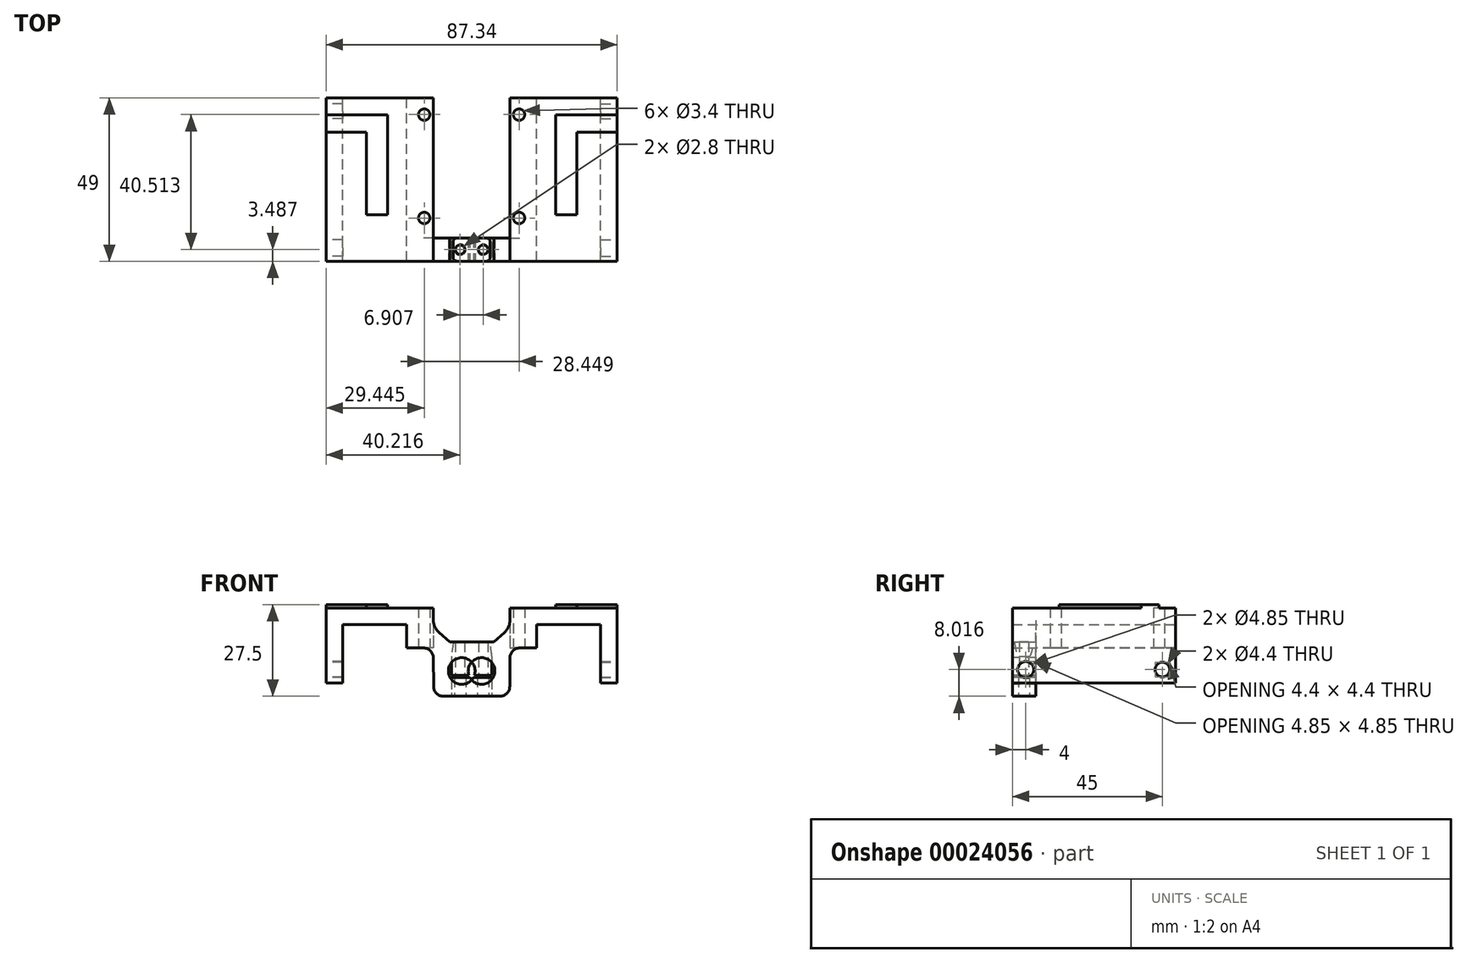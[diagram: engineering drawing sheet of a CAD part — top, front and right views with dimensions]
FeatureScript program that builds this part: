
annotation { "Feature Type Name" : "Feature", "Feature Type Description" : "" }
export const myFeature = defineFeature(function(context is Context, id is Id, definition is map)
    precondition{}
    {
        {
            var Q0;
            Q0=qCreatedBy(makeId("Front.planeOp"),FACE);
            var sketch = newSketch(context, id + "F0", { "sketchPlane" : qUnion([Q0])});
            skLineSegment(sketch, "E0", {"start": v(-18.67, 7.33) * mm, "end": v(-18.67, 29.8) * mm});
            skLineSegment(sketch, "E1", {"start": v(-18.67, 29.8) * mm, "end": v(13.53, 29.8) * mm});
            skLineSegment(sketch, "E2", {"start": v(13.53, 29.8) * mm, "end": v(13.53, 23.9) * mm});
            skLineSegment(sketch, "E3", {"start": v(5.53, 17.8) * mm, "end": v(5.53, 24.8) * mm});
            skLineSegment(sketch, "E4", {"start": v(5.53, 24.8) * mm, "end": v(-13.67, 24.8) * mm});
            skLineSegment(sketch, "E5", {"start": v(-13.67, 24.8) * mm, "end": v(-13.67, 7.33) * mm});
            skLineSegment(sketch, "E6", {"start": v(-13.67, 7.33) * mm, "end": v(-18.67, 7.33) * mm});
            skLineSegment(sketch, "E7", {"start": v(13.53, 23.9) * mm, "end": v(13.53, 17.8) * mm});
            skLineSegment(sketch, "E8", {"start": v(13.53, 17.8) * mm, "end": v(5.53, 17.8) * mm});
            skLineSegment(sketch, "E9", {"start": v(13.53, 23.9) * mm, "end": v(13.53, 23.9) * mm});
            skLineSegment(sketch, "E10", {"start": v(31.08, 15.31) * mm, "end": v(31.08, 9.01) * mm});
            skLineSegment(sketch, "E11", {"start": v(31.08, 9.01) * mm, "end": v(23.88, 9.01) * mm});
            skLineSegment(sketch, "E12", {"start": v(23.88, 9.61) * mm, "end": v(23.88, 9.01) * mm});
            skLineSegment(sketch, "E13", {"start": v(23.88, 9.61) * mm, "end": v(31.08, 9.61) * mm});
            skLineSegment(sketch, "E14", {"start": v(31.08, 9.61) * mm, "end": v(31.08, 3.31) * mm});
            skLineSegment(sketch, "E15", {"start": v(31.08, 3.31) * mm, "end": v(13.58, 3.31) * mm});
            skLineSegment(sketch, "E16", {"start": v(13.58, 3.31) * mm, "end": v(13.53, 17.8) * mm});
            skLineSegment(sketch, "E17", {"start": v(31.08, 15.31) * mm, "end": v(23.28, 15.31) * mm});
            skLineSegment(sketch, "E18", {"start": v(23.28, 15.31) * mm, "end": v(13.53, 23.9) * mm});
            skLineSegment(sketch, "E19", {"start": v(18.4, 19.61) * mm, "end": v(30.5, 19.61) * mm});
            skPoint(sketch, "E19.endSnap0", {"position": v(18.4, 19.61) * mm});
            skLineSegment(sketch, "E20", {"start": v(30.5, 19.61) * mm, "end": v(31.08, 15.31) * mm});
            skSolve(sketch);
        }
        {
            var Q0;
            Q0=makeQuery(id+"F0.imprint","IMPRINT",FACE,{"disambiguationData":[TD([[makeQuery(id+"F0.imprint","IMPRINT",EDGE,{"derivedFrom":sQuery(id+"F0.wireOp",EDGE,"E0")}),-1.0]])]});
            var Q1;
            {var subQ2=sQuery(id+"F0.wireOp",EDGE,"69cbcc5d-e0c3-48db-8baf-3487a8abab7d");Q1=makeQuery(id+"F0.imprint","IMPRINT",FACE,{"disambiguationData":[TD([[makeQuery(id+"F0.imprint","IMPRINT",EDGE,{"derivedFrom":subQ2}),-1.0]])]});}
            var Q2;
            Q2=makeQuery(id+"F0.imprint","IMPRINT",FACE,{"disambiguationData":[TD([[makeQuery(id+"F0.imprint","IMPRINT",EDGE,{"derivedFrom":sQuery(id+"F0.wireOp",EDGE,"E7")}),1.0]])]});
            var Q3;
            {var subQ2=sQuery(id+"F0.wireOp",EDGE,"E17");Q3=makeQuery(id+"F0.imprint","IMPRINT",FACE,{"disambiguationData":[TD([[makeQuery(id+"F0.imprint","IMPRINT",EDGE,{"derivedFrom":subQ2}),-1.0]])]});}
            extrude(context, id + "F1", {"entities" : qUnion([Q0, Q1, Q2, Q3]), "depth" : 7 * mm});
        }
        {
            var Q0;
            Q0=makeQuery(id+"F0.imprint","IMPRINT",FACE,{"disambiguationData":[TD([[makeQuery(id+"F0.imprint","IMPRINT",EDGE,{"derivedFrom":sQuery(id+"F0.wireOp",EDGE,"E0")}),-1.0]])]});
            extrude(context, id + "F2", {"entities" : qUnion([Q0]), "operationType" : NewBodyOperationType.ADD, "oppositeDirection" : true, "depth" : 42 * mm});
        }
        {
            var Q0;
            {var subQ0=sQuery(id+"F0.wireOp",EDGE,"E8");Q0=makeQuery(id+"F2.boolean.opBoolean","MERGE",FACE,{"derivedFrom":[makeQuery(id+"F1.opExtrude","SWEPT_FACE",FACE,{"disambiguationData":[OSD([subQ0])]}),makeQuery(id+"F2.opExtrude","SWEPT_FACE",FACE,{"disambiguationData":[OSD([subQ0])]})]});}
            var sketch = newSketch(context, id + "F3", { "sketchPlane" : qUnion([Q0])});
            skCircle(sketch, "E21", {"center": v(10.78, -6) * mm, "radius": 1.7 * mm});
            skCircle(sketch, "E22", {"center": v(10.78, -37) * mm, "radius": 1.7 * mm});
            skCircle(sketch, "E23", {"center": v(26.28, -21.5) * mm, "radius": 11 * mm});
            skSolve(sketch);
        }
        {
            var Q0;
            Q0=qSketchRegion(id+"F3",true);
            extrude(context, id + "F4", {"entities" : qUnion([Q0]), "operationType" : NewBodyOperationType.REMOVE, "endBound" : BoundingType.THROUGH_ALL, "oppositeDirection" : true, "depth" : 25 * mm});
        }
        {
            var Q0;
            Q0=makeQuery(id+"F1.opExtrude","CAP_FACE",FACE,{"disambiguationData":[OSD([sQuery(id+"F0.wireOp",EDGE,"E0"),sQuery(id+"F0.wireOp",EDGE,"E1"),sQuery(id+"F0.wireOp",EDGE,"E2"),sQuery(id+"F0.wireOp",EDGE,"E3"),sQuery(id+"F0.wireOp",EDGE,"E4"),sQuery(id+"F0.wireOp",EDGE,"E5"),sQuery(id+"F0.wireOp",EDGE,"E6"),sQuery(id+"F0.wireOp",EDGE,"E8"),sQuery(id+"F0.wireOp",EDGE,"E9"),sQuery(id+"F0.wireOp",EDGE,"58f11638-63e7-4b32-8aff-a1ba3c53649b"),sQuery(id+"F0.wireOp",EDGE,"E10"),sQuery(id+"F0.wireOp",EDGE,"E11"),sQuery(id+"F0.wireOp",EDGE,"E12"),sQuery(id+"F0.wireOp",EDGE,"E13"),sQuery(id+"F0.wireOp",EDGE,"E14"),sQuery(id+"F0.wireOp",EDGE,"E15"),sQuery(id+"F0.wireOp",EDGE,"E16")])],"isStart":false});
            var sketch = newSketch(context, id + "F5", { "sketchPlane" : qUnion([Q0])});
            skCircle(sketch, "E24", {"center": v(22.03, 10.9) * mm, "radius": 4 * mm});
            skSolve(sketch);
        }
        {
            var Q0;
            Q0=qSketchRegion(id+"F5",true);
            extrude(context, id + "F6", {"entities" : qUnion([Q0]), "operationType" : NewBodyOperationType.REMOVE, "oppositeDirection" : true, "depth" : 10 * mm});
        }
        {
            var Q0;
            Q0=qSketchRegion(id+"F3",true);
            extrude(context, id + "F7", {"entities" : qUnion([Q0]), "operationType" : NewBodyOperationType.REMOVE, "endBound" : BoundingType.THROUGH_ALL, "oppositeDirection" : true, "depth" : 25 * mm});
        }
        {
            var Q0;
            Q0=makeQuery(id+"F1.opExtrude","SWEPT_FACE",FACE,{"disambiguationData":[OSD([sQuery(id+"F0.wireOp",EDGE,"E15")])]});
            var sketch = newSketch(context, id + "F8", { "sketchPlane" : qUnion([Q0])});
            skCircle(sketch, "E25", {"center": v(28.45, 3.51) * mm, "radius": 1.7 * mm});
            skCircle(sketch, "E26", {"center": v(28.45, 3.51) * mm, "radius": 1.4 * mm});
            skSolve(sketch);
        }
        {
            var Q0;
            Q0=makeQuery(id+"F8.imprint","IMPRINT",FACE,{"disambiguationData":[TD([[makeQuery(id+"F8.imprint","IMPRINT",EDGE,{"derivedFrom":sQuery(id+"F8.wireOp",EDGE,"E26")}),1.0]])]});
            extrude(context, id + "F9", {"entities" : qUnion([Q0]), "operationType" : NewBodyOperationType.REMOVE, "endBound" : BoundingType.THROUGH_ALL, "oppositeDirection" : true, "depth" : 25 * mm});
        }
        {
            var Q0;
            Q0=makeQuery(id+"F8.imprint","IMPRINT",FACE,{"disambiguationData":[TD([[makeQuery(id+"F8.imprint","IMPRINT",EDGE,{"derivedFrom":sQuery(id+"F8.wireOp",EDGE,"E25")}),1.0]])]});
            extrude(context, id + "F10", {"entities" : qUnion([Q0]), "operationType" : NewBodyOperationType.REMOVE, "endBound" : BoundingType.UP_TO_NEXT, "oppositeDirection" : true, "depth" : 25 * mm});
        }
        {
            var Q0;
            Q0=makeQuery(id+"F1.opExtrude","SWEPT_EDGE",EDGE,{"disambiguationData":[OSD([sQuery(id+"F0.wireOp",EDGE,"E2"),sQuery(id+"F0.wireOp",EDGE,"E7"),sQuery(id+"F0.wireOp",EDGE,"E18")])]});
            fillet(context, id + "F11", {"entities" : qUnion([Q0]), "radius" : 5 * mm, "tangentPropagation" : true, "allowEdgeOverflow" : false});
        }
        {
            var Q0;
            Q0=makeQuery(id+"F1.opExtrude","SWEPT_EDGE",EDGE,{"disambiguationData":[OSD([sQuery(id+"F0.wireOp",EDGE,"E7"),sQuery(id+"F0.wireOp",EDGE,"E8"),sQuery(id+"F0.wireOp",EDGE,"E16")])]});
            fillet(context, id + "F12", {"entities" : qUnion([Q0]), "radius" : 3 * mm, "tangentPropagation" : true, "allowEdgeOverflow" : false});
        }
        {
            var Q0;
            Q0=makeQuery(id+"F1.opExtrude","SWEPT_EDGE",EDGE,{"disambiguationData":[OSD([sQuery(id+"F0.wireOp",EDGE,"E15"),sQuery(id+"F0.wireOp",EDGE,"E16")])]});
            fillet(context, id + "F13", {"entities" : qUnion([Q0]), "radius" : 3 * mm, "tangentPropagation" : true, "allowEdgeOverflow" : false});
        }
        {
            var Q0;
            Q0=makeQuery(id+"F1.opExtrude","CAP_EDGE",EDGE,{"disambiguationData":[OSD([sQuery(id+"F0.wireOp",EDGE,"E10")])],"isStart":false});
            var Q1;
            Q1=makeQuery(id+"F1.opExtrude","CAP_EDGE",EDGE,{"disambiguationData":[OSD([sQuery(id+"F0.wireOp",EDGE,"E14")])],"isStart":false});
            var Q2;
            Q2=makeQuery(id+"F1.opExtrude","CAP_EDGE",EDGE,{"disambiguationData":[OSD([sQuery(id+"F0.wireOp",EDGE,"E10")])],"isStart":true});
            var Q3;
            Q3=makeQuery(id+"F1.opExtrude","CAP_EDGE",EDGE,{"disambiguationData":[OSD([sQuery(id+"F0.wireOp",EDGE,"E14")])],"isStart":true});
            fillet(context, id + "F14", {"entities" : qUnion([Q0, Q1, Q2, Q3]), "radius" : 2 * mm, "tangentPropagation" : true, "allowEdgeOverflow" : false});
        }
        {
            var Q0;
            {var subQ0=sQuery(id+"F0.wireOp",EDGE,"E0");Q0=makeQuery(id+"F2.boolean.opBoolean","MERGE",FACE,{"derivedFrom":[makeQuery(id+"F1.opExtrude","SWEPT_FACE",FACE,{"disambiguationData":[OSD([subQ0])]}),makeQuery(id+"F2.opExtrude","SWEPT_FACE",FACE,{"disambiguationData":[OSD([subQ0])]})]});}
            var sketch = newSketch(context, id + "F15", { "sketchPlane" : qUnion([Q0])});
            skCircle(sketch, "E27", {"center": v(-38, 11.33) * mm, "radius": 2.2 * mm});
            skCircle(sketch, "E28", {"center": v(3, 11.33) * mm, "radius": 2.43 * mm});
            skSolve(sketch);
        }
        {
            var Q0;
            Q0=qSketchRegion(id+"F15",true);
            extrude(context, id + "F16", {"entities" : qUnion([Q0]), "operationType" : NewBodyOperationType.REMOVE, "oppositeDirection" : true, "depth" : 6 * mm});
        }
        {
            var Q0;
            {var subQ0=sQuery(id+"F0.wireOp",EDGE,"E1");Q0=makeQuery(id+"F2.boolean.opBoolean","MERGE",FACE,{"derivedFrom":[makeQuery(id+"F1.opExtrude","SWEPT_FACE",FACE,{"disambiguationData":[OSD([subQ0])]}),makeQuery(id+"F2.opExtrude","SWEPT_FACE",FACE,{"disambiguationData":[OSD([subQ0])]})]});}
            var sketch = newSketch(context, id + "F17", { "sketchPlane" : qUnion([Q0])});
            skText(sketch, "E29", { "text": "L", "fontName": "OpenSans-Bold.ttf"});
            const initialGuessF17  = {"E29": [0.0036, 0.03693, -1, 0, 0.0302]};
            skSetInitialGuess(sketch, initialGuessF17);
            skSolve(sketch);
        }
        {
            var Q0;
            Q0=qSketchRegion(id+"F17",true);
            extrude(context, id + "F18", {"entities" : qUnion([Q0]), "operationType" : NewBodyOperationType.ADD, "depth" : 1 * mm});
        }
        {
            var Q0;
            Q0=makeQuery(id+"F1.opExtrude","SWEPT_BODY",BODY,{"disambiguationData":[OSD([sQuery(id+"F0.wireOp",EDGE,"E0"),sQuery(id+"F0.wireOp",EDGE,"E1"),sQuery(id+"F0.wireOp",EDGE,"E2"),sQuery(id+"F0.wireOp",EDGE,"E3"),sQuery(id+"F0.wireOp",EDGE,"E4"),sQuery(id+"F0.wireOp",EDGE,"E5"),sQuery(id+"F0.wireOp",EDGE,"E6"),sQuery(id+"F0.wireOp",EDGE,"E8"),sQuery(id+"F0.wireOp",EDGE,"E10"),sQuery(id+"F0.wireOp",EDGE,"E11"),sQuery(id+"F0.wireOp",EDGE,"E12"),sQuery(id+"F0.wireOp",EDGE,"E13"),sQuery(id+"F0.wireOp",EDGE,"E14"),sQuery(id+"F0.wireOp",EDGE,"E15"),sQuery(id+"F0.wireOp",EDGE,"E16"),sQuery(id+"F0.wireOp",EDGE,"E17"),sQuery(id+"F0.wireOp",EDGE,"E18")])]});
            var Q1;
            Q1=qCreatedBy(makeId("Right.planeOp"),FACE);
            mirror(context, id + "F19", {"entities" : qUnion([Q0]), "mirrorPlane" : qUnion([Q1])});
        }
        {
            var Q0;
            Q0=makeQuery(id+"F19.opPattern","COPY",BODY,{"derivedFrom":makeQuery(id+"F1.opExtrude","SWEPT_BODY",BODY,{"disambiguationData":[OSD([sQuery(id+"F0.wireOp",EDGE,"E0"),sQuery(id+"F0.wireOp",EDGE,"E1"),sQuery(id+"F0.wireOp",EDGE,"E2"),sQuery(id+"F0.wireOp",EDGE,"E3"),sQuery(id+"F0.wireOp",EDGE,"E4"),sQuery(id+"F0.wireOp",EDGE,"E5"),sQuery(id+"F0.wireOp",EDGE,"E6"),sQuery(id+"F0.wireOp",EDGE,"E8"),sQuery(id+"F0.wireOp",EDGE,"E10"),sQuery(id+"F0.wireOp",EDGE,"E11"),sQuery(id+"F0.wireOp",EDGE,"E12"),sQuery(id+"F0.wireOp",EDGE,"E13"),sQuery(id+"F0.wireOp",EDGE,"E14"),sQuery(id+"F0.wireOp",EDGE,"E15"),sQuery(id+"F0.wireOp",EDGE,"E16"),sQuery(id+"F0.wireOp",EDGE,"E17"),sQuery(id+"F0.wireOp",EDGE,"E18")])]}),"instanceName":"1"});
            transform(context, id + "F20", {"entities" : qUnion([Q0]), "transformType" : TransformType.TRANSLATION_3D, "dx" : 50 * mm, "dy" : 0 * mm, "dz" : 0 * mm, "makeCopy" : false});
        }
    });
